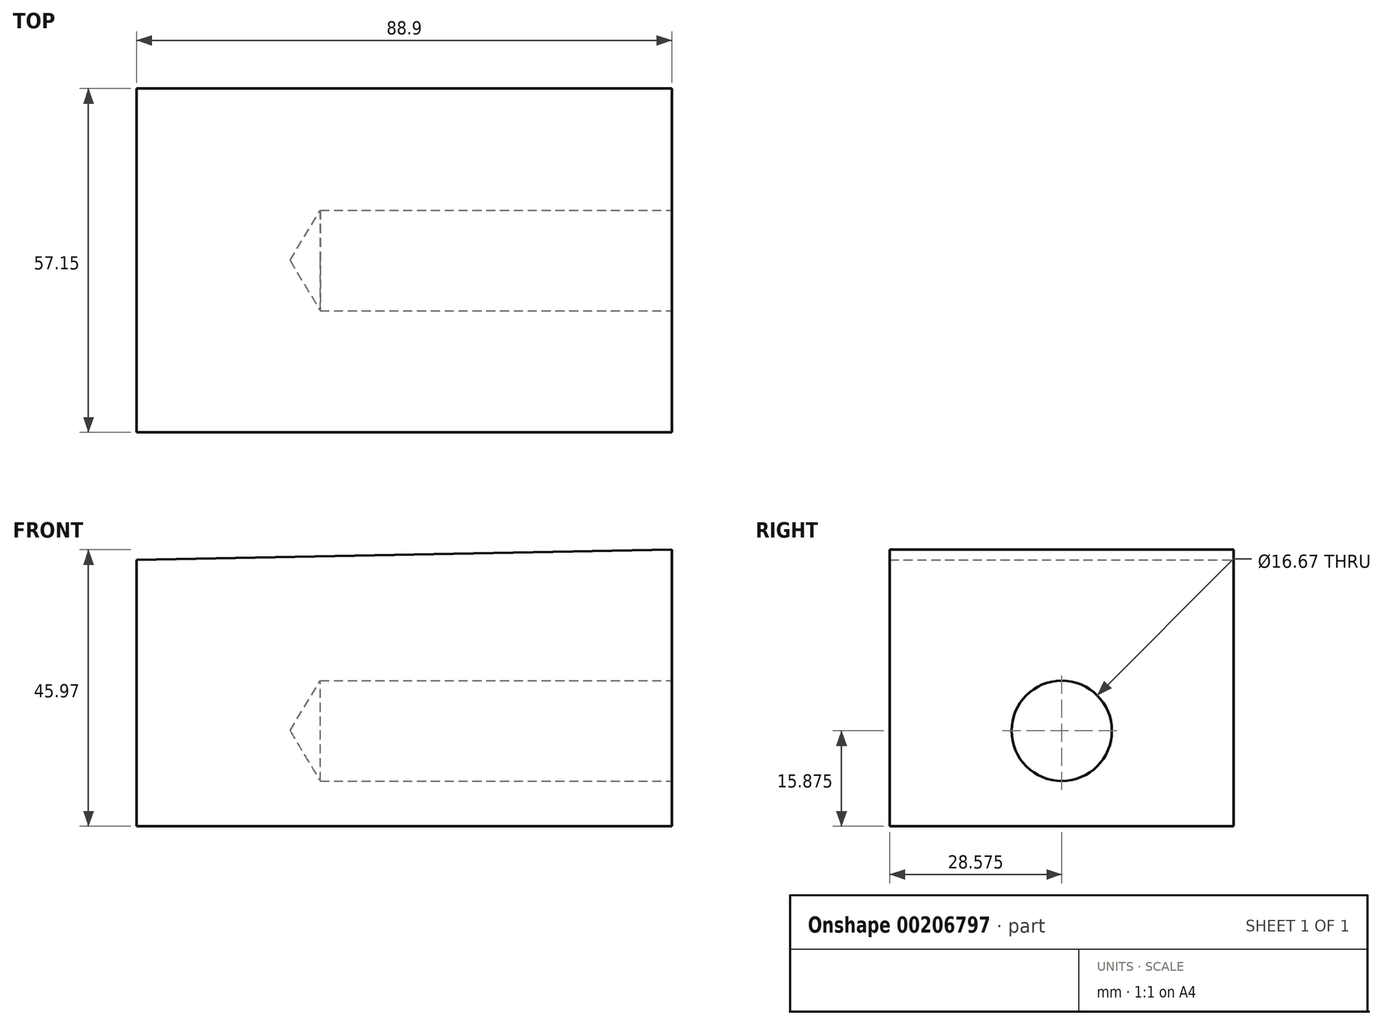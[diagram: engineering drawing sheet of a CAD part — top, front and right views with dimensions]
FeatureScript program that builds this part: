
annotation { "Feature Type Name" : "Feature", "Feature Type Description" : "" }
export const myFeature = defineFeature(function(context is Context, id is Id, definition is map)
    precondition{}
    {
        {
            var Q0;
            Q0=qCreatedBy(makeId("Front.planeOp"),FACE);
            var sketch = newSketch(context, id + "F0", { "sketchPlane" : qUnion([Q0])});
            skLineSegment(sketch, "E0", {"start": v(0, 0) * mm, "end": v(0, 44.27) * mm});
            skLineSegment(sketch, "E1", {"start": v(0, 0) * mm, "end": v(88.9, 0) * mm});
            skLineSegment(sketch, "E2", {"start": v(88.9, 0) * mm, "end": v(88.9, 45.97) * mm});
            skLineSegment(sketch, "E3", {"start": v(88.9, 45.97) * mm, "end": v(0, 44.27) * mm});
            skLineSegment(sketch, "E4", {"start": v(0, 44.27) * mm, "end": v(88.9, 44.27) * mm, "construction": true});
            skSolve(sketch);
        }
        {
            var Q0;
            Q0 = qSketchRegion(id + "F0", true);
            extrude(context, id + "F1", {"entities" : qUnion([Q0]), "offsetDistance" : 25.4 * mm, "depth" : 57.15 * mm});
        }
        {
            var Q0;
            Q0=makeQuery(id+"F1.opExtrude","SWEPT_FACE",FACE,{"disambiguationData":[OSD([sQuery(id+"F0.wireOp",EDGE,"E2")])]});
            var sketch = newSketch(context, id + "F2", { "sketchPlane" : qUnion([Q0])});
            skPoint(sketch, "E5.centerSnap0", {"position": v(-28.58, 0) * mm});
            skPoint(sketch, "E6", {"position": v(-28.58, 15.88) * mm});
            skSolve(sketch);
        }
        {
            var Q0;
            Q0=sQuery(id+"F2.wireOp",VERTEX,"E6");
            var Q1;
            Q1=makeQuery(id+"F1.opExtrude","SWEPT_BODY",BODY,{"disambiguationData":[OSD([sQuery(id+"F0.wireOp",EDGE,"E0"),sQuery(id+"F0.wireOp",EDGE,"E1"),sQuery(id+"F0.wireOp",EDGE,"E2"),sQuery(id+"F0.wireOp",EDGE,"E3")])]});
            hole(context, id + "F3", {"style" : HoleStyle.SIMPLE, "endStyle" : HoleEndStyle.BLIND, "standardTappedOrClearance" : lookupTablePath({ "standard" : "ANSI", "engagement" : "75%", "pitch" : "10 tpi", "size" : "3/4", "type" : "Tapped" }), "standardBlindInLast" : lookupTablePath({ "standard" : "ANSI", "engagement" : "75%", "pitch" : "10 tpi", "size" : "3/4", "type" : "Tapped" }), "holeDiameter" : 16.67 * mm, "showTappedDepth" : true, "holeDepth" : 58.42 * mm, "tappedDepth" : 50.8 * mm, "tapClearance" : 3, "startFromSketch" : true, "locations" : qUnion([Q0]), "scope" : qUnion([Q1]), "majorDiameter" : 19.05 * mm});
        }
    });
